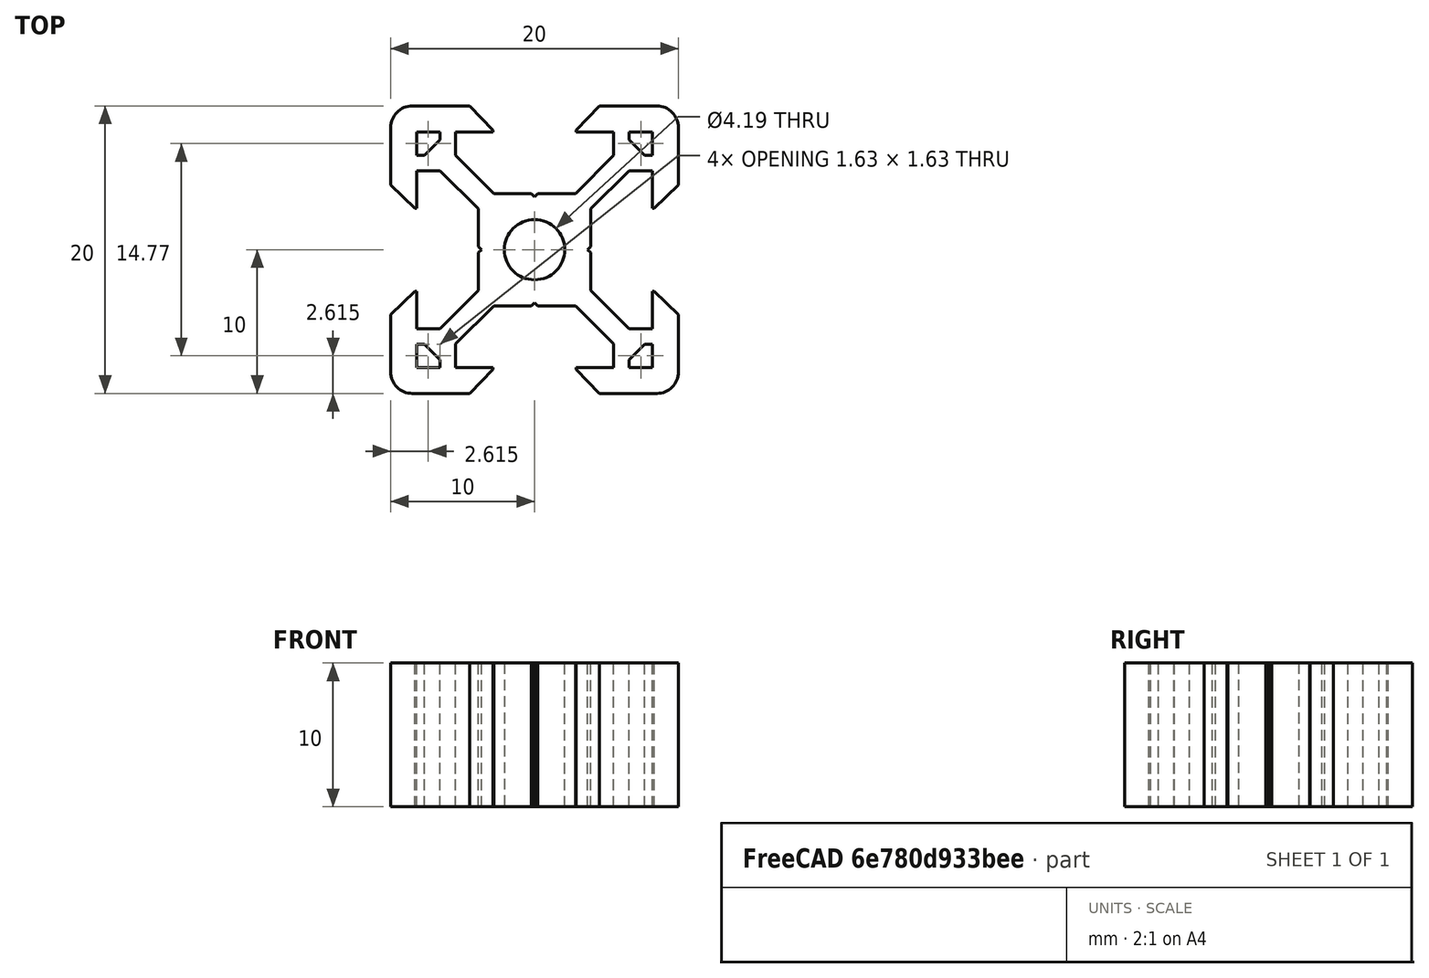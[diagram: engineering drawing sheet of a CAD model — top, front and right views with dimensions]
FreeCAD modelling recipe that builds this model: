
FCSTD DOCUMENT  (FreeCAD 0.15R4344 (Git))
Label: v-slot-profile
License: CC-BY 3.0
LicenseURL: http://creativecommons.org/licenses/by/3.0/
objects: Part::Extrusion×6, Part::Part2DObjectPython×5, Part::Cut×5, Part::Feature×1, Raytracing::LuxFeature×1, Raytracing::LuxProject×1
note: 17 computed .brp shape members not serialized (recipe doc carries the construction recipe); baked Part::Feature solids carry a one-line shape summary decoded from their .brp

FEATURE [Part::Part2DObjectPython] Circle001  # Draft 2D object (typed FeaturePython)
  FirstAngle = 0
  LastAngle = 0
  MakeFace = false
  Radius = 2.09616
FEATURE [Part::Part2DObjectPython] DWire008  # Draft 2D object (typed FeaturePython)
  ChamferSize = 0
  Closed = true
  End = (-6.57,-7.66,0)
  FilletRadius = 0
  MakeFace = false
  Points = (7) [(-6.57,-8.2,0),(-7.03106,-8.2,0),(-8.2,-8.2,0),(-8.2,-7.03106,0),(-8.2,-6.57,0),(-7.66,-6.57,0),(-6.57,-7.66,0)]
  Start = (-6.57,-8.2,0)
FEATURE [Part::Feature] Sketch001
  shape: bbox 20 x 20 x 2e-07 mm, 0 faces, 0 solids (baked)
FEATURE [Part::Part2DObjectPython] DWire009  # Draft 2D object (typed FeaturePython)
  ChamferSize = 0
  Closed = true
  End = (8.2,6.57,0)
  FilletRadius = 0
  MakeFace = false
  Points = (7) [(8.2,7.03106,0),(8.2,8.2,0),(7.03106,8.2,0),(6.57,8.2,0),(6.57,7.66,0),(7.66,6.57,0),(8.2,6.57,0)]
  Start = (8.2,7.03106,0)
FEATURE [Part::Part2DObjectPython] DWire010  # Draft 2D object (typed FeaturePython)
  ChamferSize = 0
  Closed = true
  End = (7.66,-6.57,0)
  FilletRadius = 0
  MakeFace = false
  Points = (7) [(8.2,-6.57,0),(8.2,-7.03106,0),(8.2,-8.2,0),(7.03106,-8.2,0),(6.57,-8.2,0),(6.57,-7.66,0),(7.66,-6.57,0)]
  Start = (8.2,-6.57,0)
FEATURE [Part::Part2DObjectPython] DWire011  # Draft 2D object (typed FeaturePython)
  ChamferSize = 0
  Closed = true
  End = (-7.66,6.57,0)
  FilletRadius = 0
  MakeFace = false
  Points = (7) [(-8.2,6.57,0),(-8.2,7.03106,0),(-8.2,8.2,0),(-7.03106,8.2,0),(-6.57,8.2,0),(-6.57,7.66,0),(-7.66,6.57,0)]
  Start = (-8.2,6.57,0)
FEATURE [Part::Extrusion] Extrude
  Base = -> Sketch001
  Dir = (0,0,10)
  Solid = true
FEATURE [Part::Extrusion] Extrude001
  Base = -> Circle001
  Dir = (0,0,10)
  Solid = true
FEATURE [Part::Extrusion] Extrude002
  Base = -> DWire008
  Dir = (0,0,10)
  Solid = true
FEATURE [Part::Extrusion] Extrude003
  Base = -> DWire009
  Dir = (0,0,10)
  Solid = true
FEATURE [Part::Extrusion] Extrude004
  Base = -> DWire010
  Dir = (0,0,10)
  Solid = true
FEATURE [Part::Extrusion] Extrude005
  Base = -> DWire011
  Dir = (0,0,10)
  Solid = true
FEATURE [Part::Cut] Cut
  Base = -> Extrude
  Tool = -> Extrude001
FEATURE [Part::Cut] Cut001
  Base = -> Cut
  Tool = -> Extrude005
FEATURE [Part::Cut] Cut002
  Base = -> Cut001
  Tool = -> Extrude004
FEATURE [Part::Cut] Cut003
  Base = -> Cut002
  Tool = -> Extrude003
FEATURE [Part::Cut] Cut004  label="v-slot-20x20"
  Base = -> Cut003
  Tool = -> Extrude002
FEATURE [Raytracing::LuxFeature] Cut004_View
  Result = <blob: 32134 chars omitted>
  Source = -> Cut004
FEATURE [Raytracing::LuxProject] LuxProject
  Camera = # declares positon and view direction\n# Generated by FreeCAD (http://www.freecadweb.org/)\nLookAt 38.0647 -31.7456 71.5003 7.62939e-06 0 -7.62939e-06 -0.53764 0.626449 0.564362
  Group = -> [Cut004_View]
  Template = /Applications/FreeCAD.app/Contents/data/Mod/Raytracing/Templates/LuxOutdoor.lxs
